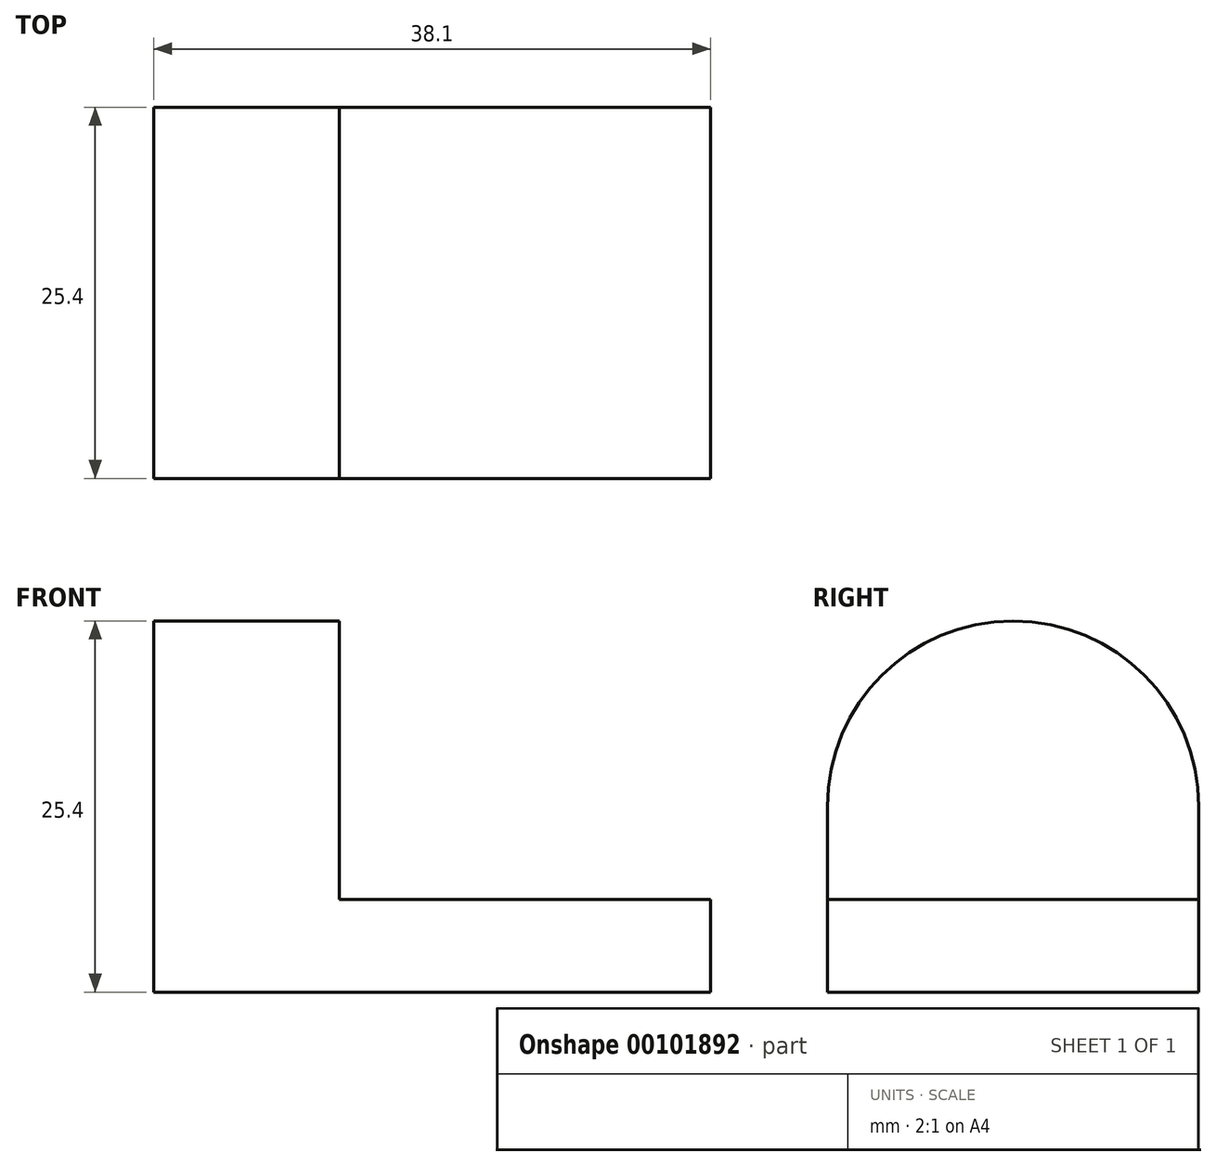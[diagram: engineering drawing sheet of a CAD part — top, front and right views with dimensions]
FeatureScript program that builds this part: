
annotation { "Feature Type Name" : "Feature", "Feature Type Description" : "" }
export const myFeature = defineFeature(function(context is Context, id is Id, definition is map)
    precondition{}
    {
        {
            var Q0;
            Q0=qCreatedBy(makeId("Right.planeOp"),FACE);
            var sketch = newSketch(context, id + "F0", { "sketchPlane" : qUnion([Q0])});
            skLineSegment(sketch, "E0", {"start": v(0, 0) * mm, "end": v(25.4, 0) * mm});
            skLineSegment(sketch, "E1", {"start": v(25.4, 0) * mm, "end": v(25.4, 6.35) * mm});
            skLineSegment(sketch, "E2", {"start": v(25.4, 6.35) * mm, "end": v(0, 6.35) * mm});
            skLineSegment(sketch, "E3", {"start": v(0, 6.35) * mm, "end": v(0, 0) * mm});
            skLineSegment(sketch, "E4", {"start": v(0, 6.35) * mm, "end": v(0, 12.7) * mm});
            skLineSegment(sketch, "E5", {"start": v(25.4, 6.35) * mm, "end": v(25.4, 12.7) * mm});
            skArc(sketch, "E6", {"start": v(0, 12.7) * mm, "mid": v(12.7, 25.4) * mm, "end": v(25.4, 12.7) * mm});
            skSolve(sketch);
        }
        {
            var Q0;
            Q0=makeQuery(id+"F0.imprint","IMPRINT",FACE,{"disambiguationData":[TD([[makeQuery(id+"F0.imprint","IMPRINT",EDGE,{"derivedFrom":sQuery(id+"F0.wireOp",EDGE,"E2")}),-1.0]])]});
            var Q1;
            Q1=makeQuery(id+"F0.imprint","IMPRINT",FACE,{"disambiguationData":[TD([[makeQuery(id+"F0.imprint","IMPRINT",EDGE,{"derivedFrom":sQuery(id+"F0.wireOp",EDGE,"E0")}),1.0]])]});
            extrude(context, id + "F1", {"entities" : qUnion([Q0, Q1]), "endBound" : BoundingType.SYMMETRIC, "depth" : 38.1 * mm});
        }
        {
            var Q0;
            Q0=qCreatedBy(makeId("Right.planeOp"),FACE);
            var sketch = newSketch(context, id + "F2", { "sketchPlane" : qUnion([Q0])});
            skArc(sketch, "E7", {"start": v(25.4, 12.7) * mm, "mid": v(12.7, 25.4) * mm, "end": v(0, 12.7) * mm});
            skLineSegment(sketch, "E8", {"start": v(0, 12.7) * mm, "end": v(0, 6.35) * mm});
            skLineSegment(sketch, "E9", {"start": v(25.4, 12.7) * mm, "end": v(25.4, 6.35) * mm});
            skLineSegment(sketch, "E10", {"start": v(25.4, 6.35) * mm, "end": v(0, 6.35) * mm});
            skSolve(sketch);
        }
        {
            var Q0;
            Q0 = qSketchRegion(id + "F2", true);
            extrude(context, id + "F3", {"entities" : qUnion([Q0]), "operationType" : NewBodyOperationType.REMOVE, "oppositeDirection" : true, "depth" : 6.35 * mm, "hasSecondDirection" : true, "secondDirectionBound" : SecondDirectionBoundingType.THROUGH_ALL, "secondDirectionOppositeDirection" : false, "secondDirectionDepth" : 25.4 * mm});
        }
    });
